# Revit family: Podajnik_recznikow_ZZ JET
name_source: partatom
category: Furniture
units: mm (PartAtom-declared; Revit-internal decimal feet)

## family parameters
Always vertical = Yes
Cut with Voids When Loaded = No
Host = Wall
Room Calculation Point = No
Shared = No

## types (1)
- Type 1
    Color / Kolor = Szary / transparentny (jasny)
    Depth / Glebokosc = 130 mm  [stored 0.426509 ft]
    Description = Podajnik na ręczniki ZZ JET to naścienny, transparentny model, który doskonale sprawdzi się w często uczęszczanych kuchniach i łazienkach. Wytworzono go z odpornego na uszkodzenia plastiku ABS. Przezroczysta obudowa umożliwia łatwą kontrolę ilość ręczników wewnątrz pojemnika, który zamykany jest na klucz. Dozownik ręczników JET jest prosty w montażu oraz bardzo wygodny w obsłudze i czyszczeniu. Wyciągnięcie z niego jednego ręcznika powoduje wysunięcie kolejnego. Funkcjonalność i uniwersalność podajnika gwarantują zadowolenie nawet najbardziej wymagających użytkowników.
    Height / Wysokosc = 270 mm  [stored 0.885827 ft]
    Manufacturer = FANECO.com
    Manufacturer code / Kod producenta = 5901764291947
    Material finish / Wykonczenie = Plastic ABS
    Model = ZZ JET
    Product code / Kod produktu = P400PGWT
    URL = https://faneco.com
    Weight / Waga = 0.7 kg
    Width / Szerokosc = 270 mm  [stored 0.885827 ft]

note: [stored X ft] marks values corroborated as IEEE doubles in the binary element streams (Revit-internal decimal feet)

## geometry (parser evidence)
native form markers: Sweep x9
no freeform markers — native parametric forms only
